# Revit family: LAMP_ARO IP54 860614X
name_source: partatom
category: Modelos genéricos
revit_build: Autodesk Revit 2015 (Build: 20140606_1530(x64)
units: mm (PartAtom-declared; Revit-internal decimal feet)

## types (3) — shared parameters
Comentarios de tipo = Availability of switching between accessories through visibility parameters when placed in a project.
Diameter = 174 mm  [stored 0.570866 ft]
Fabricante = LAMP
Grosor aro = 3 mm  [stored 0.00984252 ft]
Last update = 22/05/2020
Luminaire type = Accessory
Manufacturer URL = http://www.lamp.es
Manufacturer country = Spain
Manufacturer name = LAMP
Material Cristal = LAMP_CRISTAL ARO
Model explanation = Availability of switching between accessories through visibility parameters when placed in a project.
Product datasheet = https://www.lamp.es
Protection rating = IP54
Weight = 0.22 kg

## per-type parameters (varying)
| type | Descripción | Finish | Material Aro | Modelo | Product code |
| WHITE | DOMO 220 ACC.TRANSP GLASS WH. | Matt white | LAMP_PC Kombic Aro BL | DITRRD240W | DITRRD240W |
| GREY | DOMO 220 ACC.TRANSP GLASS GR. | Gloss grey | LAMP_PC Kombic Aro GR | DITRRD240G | DITRRD240G |
| BLACK | DOMO 220 ACC.TRANSP GLASS BK. | Matte black RAL 9011 | LAMP_PC Kombic Aro NG | DITRRD240B | DITRRD240B |

note: [stored X ft] marks values corroborated as IEEE doubles in the binary element streams (Revit-internal decimal feet)
